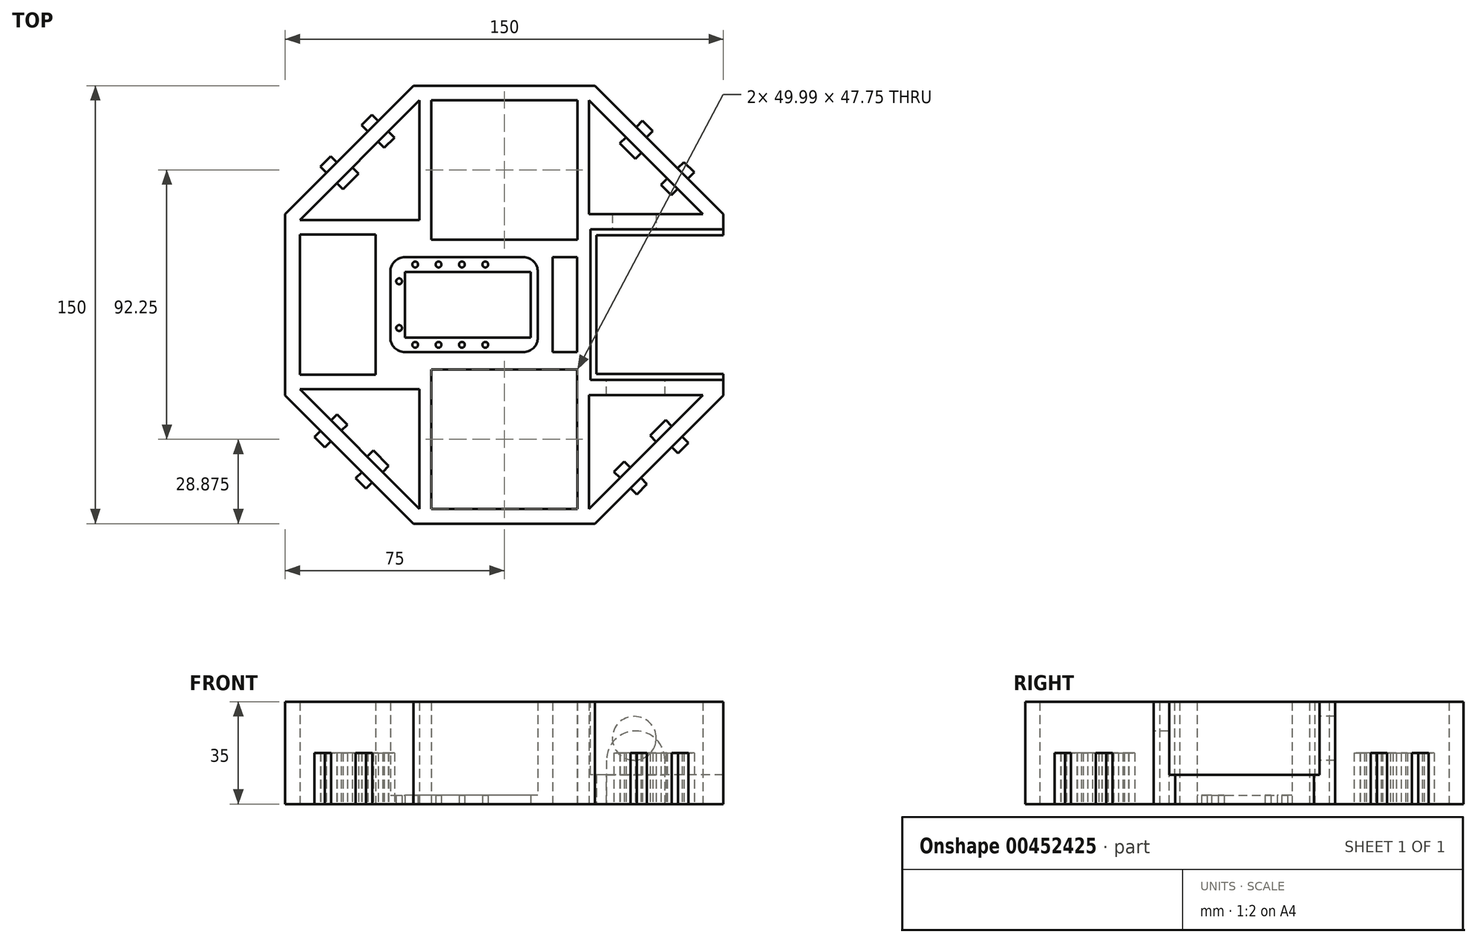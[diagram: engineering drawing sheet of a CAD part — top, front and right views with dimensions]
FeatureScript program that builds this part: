
annotation { "Feature Type Name" : "Feature", "Feature Type Description" : "" }
export const myFeature = defineFeature(function(context is Context, id is Id, definition is map)
    precondition{}
    {
        {
            var Q0;
            Q0=qCreatedBy(makeId("Top.planeOp"),FACE);
            var sketch = newSketch(context, id + "F0", { "sketchPlane" : qUnion([Q0])});
            skCircle(sketch, "E0.cCircle", {"center": v(0, 0) * mm, "radius": 75 * mm, "construction": true});
            skLineSegment(sketch, "E0.0", {"start": v(75, 31.07) * mm, "end": v(75, -31.07) * mm});
            skLineSegment(sketch, "E0.1", {"start": v(75, -31.07) * mm, "end": v(31.07, -75) * mm});
            skLineSegment(sketch, "E0.2", {"start": v(31.07, -75) * mm, "end": v(-31.07, -75) * mm});
            skLineSegment(sketch, "E0.3", {"start": v(-31.07, -75) * mm, "end": v(-75, -31.07) * mm});
            skLineSegment(sketch, "E0.4", {"start": v(-75, -31.07) * mm, "end": v(-75, 31.07) * mm});
            skLineSegment(sketch, "E0.5", {"start": v(-75, 31.07) * mm, "end": v(-31.07, 75) * mm});
            skLineSegment(sketch, "E0.6", {"start": v(-31.07, 75) * mm, "end": v(31.07, 75) * mm});
            skLineSegment(sketch, "E0.7", {"start": v(31.07, 75) * mm, "end": v(75, 31.07) * mm});
            skPoint(sketch, "E0.0.midPoint", {"position": v(75, 0) * mm});
            skLineSegment(sketch, "E1", {"start": v(0, 0) * mm, "end": v(11.5, 0) * mm, "construction": true});
            skLineSegment(sketch, "E2", {"start": v(11.5, 0) * mm, "end": v(11.5, -16.25) * mm});
            skLineSegment(sketch, "E3", {"start": v(11.5, 0) * mm, "end": v(11.5, 16.25) * mm});
            skLineSegment(sketch, "E4", {"start": v(11.5, 16.25) * mm, "end": v(-39, 16.25) * mm});
            skLineSegment(sketch, "E5", {"start": v(11.5, -16.25) * mm, "end": v(-39, -16.25) * mm});
            skLineSegment(sketch, "E6", {"start": v(-39, 16.25) * mm, "end": v(-39, -16.25) * mm});
            skSolve(sketch);
        }
        {
            var Q0;
            Q0 = qSketchRegion(id + "F0", true);
            extrude(context, id + "F1", {"entities" : qUnion([Q0]), "depth" : 35 * mm});
        }
        {
            var Q0;
            Q0=makeQuery(id+"F1.opExtrude","CAP_FACE",FACE,{"disambiguationData":[OSD([sQuery(id+"F0.wireOp",EDGE,"E0.0"),sQuery(id+"F0.wireOp",EDGE,"E0.1"),sQuery(id+"F0.wireOp",EDGE,"E0.2"),sQuery(id+"F0.wireOp",EDGE,"E0.3"),sQuery(id+"F0.wireOp",EDGE,"E0.4"),sQuery(id+"F0.wireOp",EDGE,"E0.5"),sQuery(id+"F0.wireOp",EDGE,"E0.6"),sQuery(id+"F0.wireOp",EDGE,"E0.7"),sQuery(id+"F0.wireOp",EDGE,"E2"),sQuery(id+"F0.wireOp",EDGE,"E3"),sQuery(id+"F0.wireOp",EDGE,"E4"),sQuery(id+"F0.wireOp",EDGE,"E5"),sQuery(id+"F0.wireOp",EDGE,"E6")])],"isStart":true});
            var sketch = newSketch(context, id + "F2", { "sketchPlane" : qUnion([Q0])});
            skLineSegment(sketch, "E7.0", {"start": v(31.07, 75) * mm, "end": v(-31.07, 75) * mm});
            skLineSegment(sketch, "E7.1", {"start": v(-31.07, 75) * mm, "end": v(-75, 31.07) * mm});
            skLineSegment(sketch, "E7.2", {"start": v(-75, 31.07) * mm, "end": v(-75, -31.07) * mm});
            skLineSegment(sketch, "E7.3", {"start": v(-75, -31.07) * mm, "end": v(-31.07, -75) * mm});
            skLineSegment(sketch, "E7.4", {"start": v(-31.07, -75) * mm, "end": v(31.07, -75) * mm});
            skLineSegment(sketch, "E7.5", {"start": v(31.07, -75) * mm, "end": v(75, -31.07) * mm});
            skLineSegment(sketch, "E7.6", {"start": v(75, -31.07) * mm, "end": v(75, 31.07) * mm});
            skLineSegment(sketch, "E7.7", {"start": v(75, 31.07) * mm, "end": v(31.07, 75) * mm});
            skLineSegment(sketch, "E8.0", {"start": v(-29, 70) * mm, "end": v(-70, 29) * mm});
            skLineSegment(sketch, "E8.1", {"start": v(29, 70) * mm, "end": v(-29, 70) * mm, "construction": true});
            skLineSegment(sketch, "E8.2", {"start": v(-70, 29) * mm, "end": v(-70, -29) * mm, "construction": true});
            skLineSegment(sketch, "E8.3", {"start": v(70, 29) * mm, "end": v(68, 31) * mm, "construction": true});
            skLineSegment(sketch, "E8.4", {"start": v(-70, -29) * mm, "end": v(-29, -70) * mm});
            skLineSegment(sketch, "E8.5", {"start": v(-29, -70) * mm, "end": v(29, -70) * mm, "construction": true});
            skLineSegment(sketch, "E8.6", {"start": v(29, -70) * mm, "end": v(68, -31) * mm});
            skLineSegment(sketch, "E8.7", {"start": v(70, -29) * mm, "end": v(70, 29) * mm, "construction": true});
            skLineSegment(sketch, "E9.0", {"start": v(11.5, 16.25) * mm, "end": v(-39, 16.25) * mm, "construction": true});
            skLineSegment(sketch, "E9.1", {"start": v(-39, -16.25) * mm, "end": v(-39, 16.25) * mm, "construction": true});
            skLineSegment(sketch, "E9.2", {"start": v(11.5, -16.25) * mm, "end": v(-39, -16.25) * mm, "construction": true});
            skLineSegment(sketch, "E9.3", {"start": v(11.5, 16.25) * mm, "end": v(11.5, -16.25) * mm, "construction": true});
            skLineSegment(sketch, "E10", {"start": v(-70, 29) * mm, "end": v(-29, 29) * mm});
            skLineSegment(sketch, "E11", {"start": v(-29, 70) * mm, "end": v(-29, 29) * mm});
            skLineSegment(sketch, "E12", {"start": v(29, 70) * mm, "end": v(29, 31) * mm});
            skLineSegment(sketch, "E13", {"start": v(29, 29) * mm, "end": v(70, 29) * mm, "construction": true});
            skLineSegment(sketch, "E14", {"start": v(70, -29) * mm, "end": v(29, -29) * mm, "construction": true});
            skLineSegment(sketch, "E15", {"start": v(29, -29) * mm, "end": v(29, -31) * mm, "construction": true});
            skLineSegment(sketch, "E16", {"start": v(-29, -70) * mm, "end": v(-29, -29) * mm});
            skLineSegment(sketch, "E17", {"start": v(-29, -29) * mm, "end": v(-70, -29) * mm});
            skLineSegment(sketch, "E18", {"start": v(-25, 70) * mm, "end": v(25, 70) * mm});
            skLineSegment(sketch, "E19", {"start": v(0, 0) * mm, "end": v(27.89, 0) * mm, "construction": true});
            skPoint(sketch, "E19.endSnap0", {"position": v(11.5, 0) * mm});
            skLineSegment(sketch, "E20.MirrorCS", {"start": v(-25, -70) * mm, "end": v(25, -70) * mm});
            skLineSegment(sketch, "E21", {"start": v(-44, 24) * mm, "end": v(-44, -24) * mm});
            skLineSegment(sketch, "E22.0", {"start": v(68, -31) * mm, "end": v(29, -31) * mm});
            skLineSegment(sketch, "E23", {"start": v(29, -31) * mm, "end": v(29, -70) * mm});
            skLineSegment(sketch, "E24", {"start": v(68, -31) * mm, "end": v(70, -29) * mm, "construction": true});
            skLineSegment(sketch, "E25.0", {"start": v(29, 31) * mm, "end": v(68, 31) * mm});
            skLineSegment(sketch, "E26", {"start": v(29, 31) * mm, "end": v(29, 29) * mm, "construction": true});
            skLineSegment(sketch, "E27", {"start": v(68, 31) * mm, "end": v(29, 70) * mm});
            skLineSegment(sketch, "E28", {"start": v(-44, 24) * mm, "end": v(-70, 24) * mm});
            skLineSegment(sketch, "E29", {"start": v(-44, -24) * mm, "end": v(-70, -24) * mm});
            skLineSegment(sketch, "E30", {"start": v(-70, -24) * mm, "end": v(-70, 24) * mm});
            skLineSegment(sketch, "E31", {"start": v(-25, 22.25) * mm, "end": v(24.98, 22.25) * mm});
            skLineSegment(sketch, "E32", {"start": v(-25, -22.25) * mm, "end": v(25, -22.25) * mm});
            skLineSegment(sketch, "E33", {"start": v(-25, -22.25) * mm, "end": v(-25, -70) * mm});
            skLineSegment(sketch, "E34", {"start": v(25, -22.25) * mm, "end": v(25, -70) * mm});
            skLineSegment(sketch, "E35", {"start": v(24.98, 22.25) * mm, "end": v(25, 70) * mm});
            skLineSegment(sketch, "E36", {"start": v(-25, 22.25) * mm, "end": v(-25, 70) * mm});
            skLineSegment(sketch, "E37", {"start": v(16.5, 16.25) * mm, "end": v(16.5, -16.25) * mm});
            skLineSegment(sketch, "E38", {"start": v(16.5, 16.25) * mm, "end": v(24.98, 16.25) * mm});
            skLineSegment(sketch, "E39", {"start": v(24.98, 16.25) * mm, "end": v(24.98, -16.25) * mm});
            skLineSegment(sketch, "E40", {"start": v(24.98, -16.25) * mm, "end": v(16.5, -16.25) * mm});
            skSolve(sketch);
        }
        {
            var Q0;
            Q0=makeQuery(id+"F2.imprint","IMPRINT",FACE,{"disambiguationData":[TD([[makeQuery(id+"F2.imprint","IMPRINT",EDGE,{"derivedFrom":sQuery(id+"F2.wireOp",EDGE,"E8.0")}),1.0]])]});
            var Q1;
            Q1=makeQuery(id+"F2.imprint","IMPRINT",FACE,{"disambiguationData":[TD([[makeQuery(id+"F2.imprint","IMPRINT",EDGE,{"derivedFrom":sQuery(id+"F2.wireOp",EDGE,"E8.3")}),1.0]])]});
            var Q2;
            Q2=makeQuery(id+"F2.imprint","IMPRINT",FACE,{"disambiguationData":[TD([[makeQuery(id+"F2.imprint","IMPRINT",EDGE,{"derivedFrom":sQuery(id+"F2.wireOp",EDGE,"E8.4")}),1.0]])]});
            var Q3;
            Q3=makeQuery(id+"F2.imprint","IMPRINT",FACE,{"disambiguationData":[TD([[makeQuery(id+"F2.imprint","IMPRINT",EDGE,{"derivedFrom":sQuery(id+"F2.wireOp",EDGE,"8fvEKYef-Aid4-GxJZ-9eho-uKyJXPdf4iPF")}),1.0]])]});
            var Q4;
            Q4=makeQuery(id+"F2.imprint","IMPRINT",FACE,{"disambiguationData":[TD([[makeQuery(id+"F2.imprint","IMPRINT",EDGE,{"derivedFrom":sQuery(id+"F2.wireOp",EDGE,"9003354b-389c-4ee3-9b45-5ecd4443ff8f0.MirrorCS")}),-1.0]])]});
            var Q5;
            Q5=makeQuery(id+"F2.imprint","IMPRINT",FACE,{"disambiguationData":[TD([[makeQuery(id+"F2.imprint","IMPRINT",EDGE,{"derivedFrom":sQuery(id+"F2.wireOp",EDGE,"X22rCwxT-IPlS-Nedg-AixG-TADrHZbppUWM")}),-1.0]])]});
            var Q6;
            Q6=makeQuery(id+"F2.imprint","IMPRINT",FACE,{"disambiguationData":[TD([[makeQuery(id+"F2.imprint","IMPRINT",EDGE,{"derivedFrom":sQuery(id+"F2.wireOp",EDGE,"E12")}),1.0]])]});
            var Q7;
            Q7=makeQuery(id+"F2.imprint","IMPRINT",FACE,{"disambiguationData":[TD([[makeQuery(id+"F2.imprint","IMPRINT",EDGE,{"derivedFrom":sQuery(id+"F2.wireOp",EDGE,"E8.6")}),1.0]])]});
            var Q8;
            Q8=makeQuery(id+"F2.imprint","IMPRINT",FACE,{"disambiguationData":[TD([[makeQuery(id+"F2.imprint","IMPRINT",EDGE,{"derivedFrom":sQuery(id+"F2.wireOp",EDGE,"E21")}),-1.0]])]});
            var Q9;
            Q9=makeQuery(id+"F2.imprint","IMPRINT",FACE,{"disambiguationData":[TD([[makeQuery(id+"F2.imprint","IMPRINT",EDGE,{"derivedFrom":sQuery(id+"F2.wireOp",EDGE,"E18")}),-1.0]])]});
            var Q10;
            Q10=makeQuery(id+"F2.imprint","IMPRINT",FACE,{"disambiguationData":[TD([[makeQuery(id+"F2.imprint","IMPRINT",EDGE,{"derivedFrom":sQuery(id+"F2.wireOp",EDGE,"E20.MirrorCS")}),1.0]])]});
            var Q11;
            Q11=makeQuery(id+"F2.imprint","IMPRINT",FACE,{"disambiguationData":[TD([[makeQuery(id+"F2.imprint","IMPRINT",EDGE,{"derivedFrom":sQuery(id+"F2.wireOp",EDGE,"E37")}),1.0]])]});
            extrude(context, id + "F3", {"entities" : qUnion([Q0, Q1, Q2, Q3, Q4, Q5, Q6, Q7, Q8, Q9, Q10, Q11]), "operationType" : NewBodyOperationType.REMOVE, "oppositeDirection" : true, "depth" : 36.9 * mm});
        }
        {
            var Q0;
            Q0=makeQuery(id+"F1.opExtrude","CAP_FACE",FACE,{"disambiguationData":[OSD([sQuery(id+"F0.wireOp",EDGE,"E0.0"),sQuery(id+"F0.wireOp",EDGE,"E0.1"),sQuery(id+"F0.wireOp",EDGE,"E0.2"),sQuery(id+"F0.wireOp",EDGE,"E0.3"),sQuery(id+"F0.wireOp",EDGE,"E0.4"),sQuery(id+"F0.wireOp",EDGE,"E0.5"),sQuery(id+"F0.wireOp",EDGE,"E0.6"),sQuery(id+"F0.wireOp",EDGE,"E0.7"),sQuery(id+"F0.wireOp",EDGE,"E2"),sQuery(id+"F0.wireOp",EDGE,"E3"),sQuery(id+"F0.wireOp",EDGE,"E4"),sQuery(id+"F0.wireOp",EDGE,"E5"),sQuery(id+"F0.wireOp",EDGE,"E6")])],"isStart":true});
            var sketch = newSketch(context, id + "F4", { "sketchPlane" : qUnion([Q0])});
            skLineSegment(sketch, "E41.0", {"start": v(-39, -16.25) * mm, "end": v(-39, 16.25) * mm});
            skLineSegment(sketch, "E41.1", {"start": v(11.5, 16.25) * mm, "end": v(-39, 16.25) * mm});
            skLineSegment(sketch, "E41.2", {"start": v(11.5, -16.25) * mm, "end": v(-39, -16.25) * mm});
            skLineSegment(sketch, "E41.3", {"start": v(11.5, 16.25) * mm, "end": v(11.5, -16.25) * mm});
            skLineSegment(sketch, "E42.0", {"start": v(9, -11.25) * mm, "end": v(-34, -11.25) * mm});
            skLineSegment(sketch, "E42.1", {"start": v(-34, -11.25) * mm, "end": v(-34, 11.25) * mm});
            skLineSegment(sketch, "E42.2", {"start": v(9, 11.25) * mm, "end": v(-34, 11.25) * mm});
            skLineSegment(sketch, "E43", {"start": v(-39, 13.75) * mm, "end": v(-30.5, 13.75) * mm, "construction": true});
            skLineSegment(sketch, "E44", {"start": v(-30.5, 13.75) * mm, "end": v(-22.5, 13.75) * mm, "construction": true});
            skLineSegment(sketch, "E45", {"start": v(-22.5, 13.75) * mm, "end": v(-14.5, 13.75) * mm, "construction": true});
            skLineSegment(sketch, "E46", {"start": v(-14.5, 13.75) * mm, "end": v(-6.5, 13.75) * mm, "construction": true});
            skCircle(sketch, "E47", {"center": v(-30.5, 13.75) * mm, "radius": 1 * mm});
            skCircle(sketch, "E48", {"center": v(-22.5, 13.75) * mm, "radius": 1 * mm});
            skCircle(sketch, "E49", {"center": v(-14.5, 13.75) * mm, "radius": 1 * mm});
            skCircle(sketch, "E50", {"center": v(-6.5, 13.75) * mm, "radius": 1 * mm});
            skLineSegment(sketch, "E51", {"start": v(-39, 0) * mm, "end": v(-36, 0) * mm, "construction": true});
            skPoint(sketch, "E51.endSnap0", {"position": v(-39, 0) * mm});
            skLineSegment(sketch, "E52", {"start": v(-36, 0) * mm, "end": v(-36, 8) * mm, "construction": true});
            skLineSegment(sketch, "E53", {"start": v(-36, 0) * mm, "end": v(-36, -8) * mm, "construction": true});
            skLineSegment(sketch, "E54.MirrorCS", {"start": v(-39, -13.75) * mm, "end": v(-30.5, -13.75) * mm, "construction": true});
            skLineSegment(sketch, "E55.MirrorCS", {"start": v(-14.5, -13.75) * mm, "end": v(-6.5, -13.75) * mm, "construction": true});
            skCircle(sketch, "E56.MirrorC", {"center": v(-22.5, -13.75) * mm, "radius": 1 * mm});
            skCircle(sketch, "E57.MirrorC", {"center": v(-6.5, -13.75) * mm, "radius": 1 * mm});
            skCircle(sketch, "E58.MirrorC", {"center": v(-30.5, -13.75) * mm, "radius": 1 * mm});
            skLineSegment(sketch, "E59.MirrorCS", {"start": v(-30.5, -13.75) * mm, "end": v(-22.5, -13.75) * mm, "construction": true});
            skLineSegment(sketch, "E60.MirrorCS", {"start": v(-22.5, -13.75) * mm, "end": v(-14.5, -13.75) * mm, "construction": true});
            skCircle(sketch, "E61.MirrorC", {"center": v(-14.5, -13.75) * mm, "radius": 1 * mm});
            skCircle(sketch, "E62", {"center": v(-36, 8) * mm, "radius": 1 * mm});
            skCircle(sketch, "E63", {"center": v(-36, -8) * mm, "radius": 1 * mm});
            skLineSegment(sketch, "E64.0", {"start": v(9, 11.25) * mm, "end": v(9, -11.25) * mm});
            skSolve(sketch);
        }
        {
            var Q0;
            Q0=makeQuery(id+"F4.imprint","IMPRINT",FACE,{"disambiguationData":[TD([[makeQuery(id+"F4.imprint","IMPRINT",EDGE,{"derivedFrom":sQuery(id+"F4.wireOp",EDGE,"E41.0")}),-1.0]])]});
            extrude(context, id + "F5", {"entities" : qUnion([Q0]), "operationType" : NewBodyOperationType.ADD, "oppositeDirection" : true, "depth" : 3 * mm});
        }
        {
            var Q0;
            Q0=makeQuery(id+"F1.opExtrude","SWEPT_EDGE",EDGE,{"disambiguationData":[OSD([sQuery(id+"F0.wireOp",EDGE,"E5"),sQuery(id+"F0.wireOp",EDGE,"E6")])]});
            var Q1;
            Q1=makeQuery(id+"F1.opExtrude","SWEPT_EDGE",EDGE,{"disambiguationData":[OSD([sQuery(id+"F0.wireOp",EDGE,"E4"),sQuery(id+"F0.wireOp",EDGE,"E6")])]});
            var Q2;
            Q2=makeQuery(id+"F1.opExtrude","SWEPT_EDGE",EDGE,{"disambiguationData":[OSD([sQuery(id+"F0.wireOp",EDGE,"E3"),sQuery(id+"F0.wireOp",EDGE,"E4")])]});
            var Q3;
            Q3=makeQuery(id+"F1.opExtrude","SWEPT_EDGE",EDGE,{"disambiguationData":[OSD([sQuery(id+"F0.wireOp",EDGE,"E2"),sQuery(id+"F0.wireOp",EDGE,"E5")])]});
            fillet(context, id + "F6", {"entities" : qUnion([Q0, Q1, Q2, Q3]), "radius" : 5 * mm, "tangentPropagation" : true, "allowEdgeOverflow" : false});
        }
        {
            var Q0;
            Q0=makeQuery(id+"F1.opExtrude","CAP_FACE",FACE,{"disambiguationData":[OSD([sQuery(id+"F0.wireOp",EDGE,"E0.0"),sQuery(id+"F0.wireOp",EDGE,"E0.1"),sQuery(id+"F0.wireOp",EDGE,"E0.2"),sQuery(id+"F0.wireOp",EDGE,"E0.3"),sQuery(id+"F0.wireOp",EDGE,"E0.4"),sQuery(id+"F0.wireOp",EDGE,"E0.5"),sQuery(id+"F0.wireOp",EDGE,"E0.6"),sQuery(id+"F0.wireOp",EDGE,"E0.7"),sQuery(id+"F0.wireOp",EDGE,"E2"),sQuery(id+"F0.wireOp",EDGE,"E3"),sQuery(id+"F0.wireOp",EDGE,"E4"),sQuery(id+"F0.wireOp",EDGE,"E5"),sQuery(id+"F0.wireOp",EDGE,"E6")])],"isStart":false});
            var sketch = newSketch(context, id + "F7", { "sketchPlane" : qUnion([Q0])});
            skLineSegment(sketch, "E65.bottom", {"start": v(75, -25.75) * mm, "end": v(29.5, -25.75) * mm});
            skLineSegment(sketch, "E65.top", {"start": v(75, 25.75) * mm, "end": v(29.5, 25.75) * mm});
            skLineSegment(sketch, "E65.right", {"start": v(29.5, -25.75) * mm, "end": v(29.5, 25.75) * mm});
            skPoint(sketch, "E65.middle", {"position": v(52.25, 0) * mm});
            skPoint(sketch, "E66", {"position": v(75, 0) * mm});
            skLineSegment(sketch, "E67", {"start": v(75, 0) * mm, "end": v(52.25, 0) * mm, "construction": true});
            skSolve(sketch);
        }
        {
            var Q0;
            {var subQ0=sQuery(id+"F7.wireOp",EDGE,"E65.bottom");Q0=makeQuery(id+"F7.imprint","IMPRINT",FACE,{"disambiguationData":[TD([[makeQuery(id+"F7.imprint","IMPRINT",EDGE,{"derivedFrom":subQ0}),-1.0]])]});}
            extrude(context, id + "F8", {"entities" : qUnion([Q0]), "operationType" : NewBodyOperationType.REMOVE, "oppositeDirection" : true, "depth" : 30 * mm});
        }
        {
            var Q0;
            Q0=makeQuery(id+"F8.boolean.opBoolean","COPY",FACE,{"derivedFrom":makeQuery(id+"F8.opExtrude","CAP_FACE",FACE,{"disambiguationData":[OSD([sQuery(id+"F0.wireOp",EDGE,"E0.0"),sQuery(id+"F7.wireOp",EDGE,"E65.bottom"),sQuery(id+"F7.wireOp",EDGE,"E65.top"),sQuery(id+"F7.wireOp",EDGE,"E65.right")])],"isStart":false})});
            var sketch = newSketch(context, id + "F9", { "sketchPlane" : qUnion([Q0])});
            skLineSegment(sketch, "E68.0", {"start": v(75, 25.75) * mm, "end": v(29.5, 25.75) * mm});
            skLineSegment(sketch, "E68.1", {"start": v(29.5, -25.75) * mm, "end": v(29.5, 25.75) * mm});
            skLineSegment(sketch, "E68.2", {"start": v(75, -25.75) * mm, "end": v(29.5, -25.75) * mm});
            skLineSegment(sketch, "E69.0", {"start": v(75, -23.75) * mm, "end": v(31.5, -23.75) * mm});
            skLineSegment(sketch, "E69.1", {"start": v(31.5, -23.75) * mm, "end": v(31.5, 23.75) * mm});
            skLineSegment(sketch, "E69.2", {"start": v(75, 23.75) * mm, "end": v(31.5, 23.75) * mm});
            skLineSegment(sketch, "E70", {"start": v(75, 23.75) * mm, "end": v(75, 25.75) * mm});
            skLineSegment(sketch, "E71", {"start": v(75, -23.75) * mm, "end": v(75, -25.75) * mm});
            skSolve(sketch);
        }
        {
            var Q0;
            Q0=makeQuery(id+"F9.imprint","IMPRINT",FACE,{"disambiguationData":[TD([[makeQuery(id+"F9.imprint","IMPRINT",EDGE,{"derivedFrom":sQuery(id+"F9.wireOp",EDGE,"E68.0")}),1.0]])]});
            extrude(context, id + "F10", {"entities" : qUnion([Q0]), "operationType" : NewBodyOperationType.ADD, "depth" : 5 * mm});
        }
        {
            var Q0;
            Q0=makeQuery(id+"F8.boolean.opBoolean","COPY",FACE,{"derivedFrom":makeQuery(id+"F8.opExtrude","SWEPT_FACE",FACE,{"disambiguationData":[OSD([sQuery(id+"F7.wireOp",EDGE,"E65.bottom")])]})});
            var sketch = newSketch(context, id + "F11", { "sketchPlane" : qUnion([Q0])});
            skLineSegment(sketch, "E72.0", {"start": v(-68, 35) * mm, "end": v(-68, 0) * mm, "construction": true});
            skLineSegment(sketch, "E73", {"start": v(-55, 10) * mm, "end": v(-55, 25) * mm});
            skLineSegment(sketch, "E74", {"start": v(-55, 25) * mm, "end": v(-35, 25) * mm});
            skLineSegment(sketch, "E75", {"start": v(-35, 25) * mm, "end": v(-35, 10) * mm});
            skLineSegment(sketch, "E76", {"start": v(-35, 10) * mm, "end": v(-55, 10) * mm});
            skSolve(sketch);
        }
        {
            var Q0;
            Q0=makeQuery(id+"F11.imprint","IMPRINT",FACE,{"disambiguationData":[TD([[makeQuery(id+"F11.imprint","IMPRINT",EDGE,{"derivedFrom":sQuery(id+"F11.wireOp",EDGE,"E73")}),-1.0]])]});
            extrude(context, id + "F12", {"entities" : qUnion([Q0]), "operationType" : NewBodyOperationType.REMOVE, "oppositeDirection" : true, "depth" : 11.4 * mm});
        }
        {
            var Q0;
            Q0=makeQuery(id+"F12.boolean.opBoolean","COPY",EDGE,{"derivedFrom":makeQuery(id+"F12.opExtrude","SWEPT_EDGE",EDGE,{"disambiguationData":[OSD([sQuery(id+"F11.wireOp",EDGE,"E73"),sQuery(id+"F11.wireOp",EDGE,"E74")])]})});
            var Q1;
            Q1=makeQuery(id+"F12.boolean.opBoolean","COPY",EDGE,{"derivedFrom":makeQuery(id+"F12.opExtrude","SWEPT_EDGE",EDGE,{"disambiguationData":[OSD([sQuery(id+"F11.wireOp",EDGE,"E74"),sQuery(id+"F11.wireOp",EDGE,"E75")])]})});
            fillet(context, id + "F13", {"entities" : qUnion([Q0, Q1]), "radius" : 10 * mm, "tangentPropagation" : true, "allowEdgeOverflow" : false});
        }
        {
            var Q0;
            Q0=makeQuery(id+"F12.boolean.opBoolean","MERGE",FACE,{"derivedFrom":[makeQuery(id+"F10.opExtrude","CAP_FACE",FACE,{"disambiguationData":[OSD([sQuery(id+"F9.wireOp",EDGE,"E68.0"),sQuery(id+"F9.wireOp",EDGE,"E68.1"),sQuery(id+"F9.wireOp",EDGE,"E68.2"),sQuery(id+"F9.wireOp",EDGE,"E69.0"),sQuery(id+"F9.wireOp",EDGE,"E69.1"),sQuery(id+"F9.wireOp",EDGE,"E69.2"),sQuery(id+"F9.wireOp",EDGE,"E70"),sQuery(id+"F9.wireOp",EDGE,"E71")])],"isStart":false}),makeQuery(id+"F12.opExtrude","SWEPT_FACE",FACE,{"disambiguationData":[OSD([sQuery(id+"F11.wireOp",EDGE,"E76")])]})]});
            var sketch = newSketch(context, id + "F14", { "sketchPlane" : qUnion([Q0])});
            skLineSegment(sketch, "E77", {"start": v(35, -31) * mm, "end": v(35, -25.75) * mm});
            skLineSegment(sketch, "E78", {"start": v(35, -25.75) * mm, "end": v(55, -25.75) * mm});
            skLineSegment(sketch, "E79", {"start": v(55, -25.75) * mm, "end": v(55, -31) * mm});
            skLineSegment(sketch, "E80", {"start": v(55, -31) * mm, "end": v(35, -31) * mm});
            skSolve(sketch);
        }
        {
            var Q0;
            Q0=makeQuery(id+"F14.imprint","IMPRINT",FACE,{"disambiguationData":[TD([[makeQuery(id+"F14.imprint","IMPRINT",EDGE,{"derivedFrom":sQuery(id+"F14.wireOp",EDGE,"E77")}),-1.0]])]});
            extrude(context, id + "F15", {"entities" : qUnion([Q0]), "operationType" : NewBodyOperationType.REMOVE, "oppositeDirection" : true, "depth" : 25 * mm});
        }
        {
            var Q0;
            Q0=makeQuery(id+"F8.boolean.opBoolean","COPY",FACE,{"derivedFrom":makeQuery(id+"F8.opExtrude","SWEPT_FACE",FACE,{"disambiguationData":[OSD([sQuery(id+"F7.wireOp",EDGE,"E65.top")])]})});
            var sketch = newSketch(context, id + "F16", { "sketchPlane" : qUnion([Q0])});
            skLineSegment(sketch, "E81", {"start": v(29.5, 22.5) * mm, "end": v(44.5, 22.5) * mm, "construction": true});
            skCircle(sketch, "E82", {"center": v(44.5, 22.5) * mm, "radius": 7.5 * mm});
            skSolve(sketch);
        }
        {
            var Q0;
            Q0=makeQuery(id+"F16.imprint","IMPRINT",FACE,{"disambiguationData":[TD([[makeQuery(id+"F16.imprint","IMPRINT",EDGE,{"derivedFrom":sQuery(id+"F16.wireOp",EDGE,"E82")}),1.0]])]});
            extrude(context, id + "F17", {"entities" : qUnion([Q0]), "operationType" : NewBodyOperationType.REMOVE, "oppositeDirection" : true, "depth" : 7.7 * mm});
        }
        {
            var Q0;
            Q0=makeQuery(id+"F8.boolean.opBoolean","COPY",FACE,{"derivedFrom":makeQuery(id+"F8.opExtrude","CAP_FACE",FACE,{"disambiguationData":[OSD([sQuery(id+"F0.wireOp",EDGE,"E0.0"),sQuery(id+"F7.wireOp",EDGE,"E65.bottom"),sQuery(id+"F7.wireOp",EDGE,"E65.top"),sQuery(id+"F7.wireOp",EDGE,"E65.right")])],"isStart":false})});
            extrude(context, id + "F18", {"entities" : qUnion([Q0]), "operationType" : NewBodyOperationType.REMOVE, "oppositeDirection" : true, "depth" : 25 * mm});
        }
        {
            var Q0;
            Q0=qCreatedBy(makeId("Top.planeOp"),FACE);
            var sketch = newSketch(context, id + "F19", { "sketchPlane" : qUnion([Q0])});
            skPoint(sketch, "E83.0", {"position": v(48.5, -50.5) * mm});
            skLineSegment(sketch, "E84.0", {"start": v(68, -31) * mm, "end": v(29, -70) * mm, "construction": true});
            skLineSegment(sketch, "E85", {"start": v(43.2, -55.8) * mm, "end": v(41.07, -53.68) * mm});
            skLineSegment(sketch, "E86", {"start": v(52.03, -46.96) * mm, "end": v(49.91, -44.84) * mm});
            skLineSegment(sketch, "E87", {"start": v(41.07, -53.68) * mm, "end": v(37.54, -57.21) * mm});
            skLineSegment(sketch, "E88", {"start": v(37.54, -57.21) * mm, "end": v(39.66, -59.34) * mm});
            skLineSegment(sketch, "E89", {"start": v(49.91, -44.84) * mm, "end": v(55.21, -39.54) * mm});
            skLineSegment(sketch, "E90", {"start": v(55.21, -39.54) * mm, "end": v(57.34, -41.66) * mm});
            skLineSegment(sketch, "E91", {"start": v(48.5, -50.5) * mm, "end": v(52.03, -54.03) * mm, "construction": true});
            skLineSegment(sketch, "E92.0", {"start": v(75, -31.07) * mm, "end": v(31.07, -75) * mm, "construction": true});
            skLineSegment(sketch, "E93", {"start": v(43.2, -55.8) * mm, "end": v(39.66, -59.34) * mm});
            skLineSegment(sketch, "E94", {"start": v(52.03, -46.96) * mm, "end": v(57.34, -41.66) * mm});
            skLineSegment(sketch, "E95", {"start": v(46.73, -59.34) * mm, "end": v(48.85, -61.46) * mm});
            skLineSegment(sketch, "E96", {"start": v(48.85, -61.46) * mm, "end": v(45.32, -65) * mm});
            skLineSegment(sketch, "E97", {"start": v(45.32, -65) * mm, "end": v(43.2, -62.87) * mm});
            skLineSegment(sketch, "E98", {"start": v(43.2, -62.87) * mm, "end": v(46.73, -59.34) * mm});
            skLineSegment(sketch, "E99", {"start": v(57.34, -48.73) * mm, "end": v(59.46, -50.85) * mm});
            skLineSegment(sketch, "E100", {"start": v(59.46, -50.85) * mm, "end": v(63, -47.32) * mm});
            skLineSegment(sketch, "E101", {"start": v(63, -47.32) * mm, "end": v(60.87, -45.2) * mm});
            skLineSegment(sketch, "E102", {"start": v(60.87, -45.2) * mm, "end": v(57.34, -48.73) * mm});
            skLineSegment(sketch, "E103.1.0", {"start": v(50.85, 59.46) * mm, "end": v(47.32, 63) * mm});
            skLineSegment(sketch, "E103.1.1", {"start": v(48.73, 57.34) * mm, "end": v(50.85, 59.46) * mm});
            skLineSegment(sketch, "E103.1.2", {"start": v(45.2, 60.87) * mm, "end": v(48.73, 57.34) * mm});
            skLineSegment(sketch, "E103.1.3", {"start": v(47.32, 63) * mm, "end": v(45.2, 60.87) * mm});
            skLineSegment(sketch, "E103.1.4", {"start": v(62.87, 43.2) * mm, "end": v(59.34, 46.73) * mm});
            skLineSegment(sketch, "E103.1.5", {"start": v(59.34, 46.73) * mm, "end": v(61.46, 48.85) * mm});
            skLineSegment(sketch, "E103.1.6", {"start": v(61.46, 48.85) * mm, "end": v(65, 45.32) * mm});
            skLineSegment(sketch, "E103.1.7", {"start": v(65, 45.32) * mm, "end": v(62.87, 43.2) * mm});
            skLineSegment(sketch, "E103.1.8", {"start": v(55.8, 43.2) * mm, "end": v(53.68, 41.07) * mm});
            skLineSegment(sketch, "E103.1.9", {"start": v(53.68, 41.07) * mm, "end": v(57.21, 37.54) * mm});
            skLineSegment(sketch, "E103.1.10", {"start": v(57.21, 37.54) * mm, "end": v(59.34, 39.66) * mm});
            skLineSegment(sketch, "E103.1.11", {"start": v(55.8, 43.2) * mm, "end": v(59.34, 39.66) * mm});
            skLineSegment(sketch, "E103.1.12", {"start": v(46.96, 52.03) * mm, "end": v(44.84, 49.91) * mm});
            skLineSegment(sketch, "E103.1.13", {"start": v(44.84, 49.91) * mm, "end": v(39.54, 55.21) * mm});
            skLineSegment(sketch, "E103.1.14", {"start": v(46.96, 52.03) * mm, "end": v(41.66, 57.34) * mm});
            skLineSegment(sketch, "E103.1.15", {"start": v(39.54, 55.21) * mm, "end": v(41.66, 57.34) * mm});
            skLineSegment(sketch, "E103.2.0", {"start": v(-59.46, 50.85) * mm, "end": v(-63, 47.32) * mm});
            skLineSegment(sketch, "E103.2.1", {"start": v(-57.34, 48.73) * mm, "end": v(-59.46, 50.85) * mm});
            skLineSegment(sketch, "E103.2.2", {"start": v(-60.87, 45.2) * mm, "end": v(-57.34, 48.73) * mm});
            skLineSegment(sketch, "E103.2.3", {"start": v(-63, 47.32) * mm, "end": v(-60.87, 45.2) * mm});
            skLineSegment(sketch, "E103.2.4", {"start": v(-43.2, 62.87) * mm, "end": v(-46.73, 59.34) * mm});
            skLineSegment(sketch, "E103.2.5", {"start": v(-46.73, 59.34) * mm, "end": v(-48.85, 61.46) * mm});
            skLineSegment(sketch, "E103.2.6", {"start": v(-48.85, 61.46) * mm, "end": v(-45.32, 65) * mm});
            skLineSegment(sketch, "E103.2.7", {"start": v(-45.32, 65) * mm, "end": v(-43.2, 62.87) * mm});
            skLineSegment(sketch, "E103.2.8", {"start": v(-43.2, 55.8) * mm, "end": v(-41.07, 53.68) * mm});
            skLineSegment(sketch, "E103.2.9", {"start": v(-41.07, 53.68) * mm, "end": v(-37.54, 57.21) * mm});
            skLineSegment(sketch, "E103.2.10", {"start": v(-37.54, 57.21) * mm, "end": v(-39.66, 59.34) * mm});
            skLineSegment(sketch, "E103.2.11", {"start": v(-43.2, 55.8) * mm, "end": v(-39.66, 59.34) * mm});
            skLineSegment(sketch, "E103.2.12", {"start": v(-52.03, 46.96) * mm, "end": v(-49.91, 44.84) * mm});
            skLineSegment(sketch, "E103.2.13", {"start": v(-49.91, 44.84) * mm, "end": v(-55.21, 39.54) * mm});
            skLineSegment(sketch, "E103.2.14", {"start": v(-52.03, 46.96) * mm, "end": v(-57.34, 41.66) * mm});
            skLineSegment(sketch, "E103.2.15", {"start": v(-55.21, 39.54) * mm, "end": v(-57.34, 41.66) * mm});
            skLineSegment(sketch, "E103.3.0", {"start": v(-50.85, -59.46) * mm, "end": v(-47.32, -63) * mm});
            skLineSegment(sketch, "E103.3.1", {"start": v(-48.73, -57.34) * mm, "end": v(-50.85, -59.46) * mm});
            skLineSegment(sketch, "E103.3.2", {"start": v(-45.2, -60.87) * mm, "end": v(-48.73, -57.34) * mm});
            skLineSegment(sketch, "E103.3.3", {"start": v(-47.32, -63) * mm, "end": v(-45.2, -60.87) * mm});
            skLineSegment(sketch, "E103.3.4", {"start": v(-62.87, -43.2) * mm, "end": v(-59.34, -46.73) * mm});
            skLineSegment(sketch, "E103.3.5", {"start": v(-59.34, -46.73) * mm, "end": v(-61.46, -48.85) * mm});
            skLineSegment(sketch, "E103.3.6", {"start": v(-61.46, -48.85) * mm, "end": v(-65, -45.32) * mm});
            skLineSegment(sketch, "E103.3.7", {"start": v(-65, -45.32) * mm, "end": v(-62.87, -43.2) * mm});
            skLineSegment(sketch, "E103.3.8", {"start": v(-55.8, -43.2) * mm, "end": v(-53.68, -41.07) * mm});
            skLineSegment(sketch, "E103.3.9", {"start": v(-53.68, -41.07) * mm, "end": v(-57.21, -37.54) * mm});
            skLineSegment(sketch, "E103.3.10", {"start": v(-57.21, -37.54) * mm, "end": v(-59.34, -39.66) * mm});
            skLineSegment(sketch, "E103.3.11", {"start": v(-55.8, -43.2) * mm, "end": v(-59.34, -39.66) * mm});
            skLineSegment(sketch, "E103.3.12", {"start": v(-46.96, -52.03) * mm, "end": v(-44.84, -49.91) * mm});
            skLineSegment(sketch, "E103.3.13", {"start": v(-44.84, -49.91) * mm, "end": v(-39.54, -55.21) * mm});
            skLineSegment(sketch, "E103.3.14", {"start": v(-46.96, -52.03) * mm, "end": v(-41.66, -57.34) * mm});
            skLineSegment(sketch, "E103.3.15", {"start": v(-39.54, -55.21) * mm, "end": v(-41.66, -57.34) * mm});
            skPoint(sketch, "E103.center", {"position": v(0, 0) * mm});
            skSolve(sketch);
        }
        {
            var Q0;
            Q0 = qSketchRegion(id + "F19", true);
            extrude(context, id + "F20", {"entities" : qUnion([Q0]), "operationType" : NewBodyOperationType.ADD, "depth" : 17.5 * mm, "offsetDistance" : 25 * mm});
        }
    });
